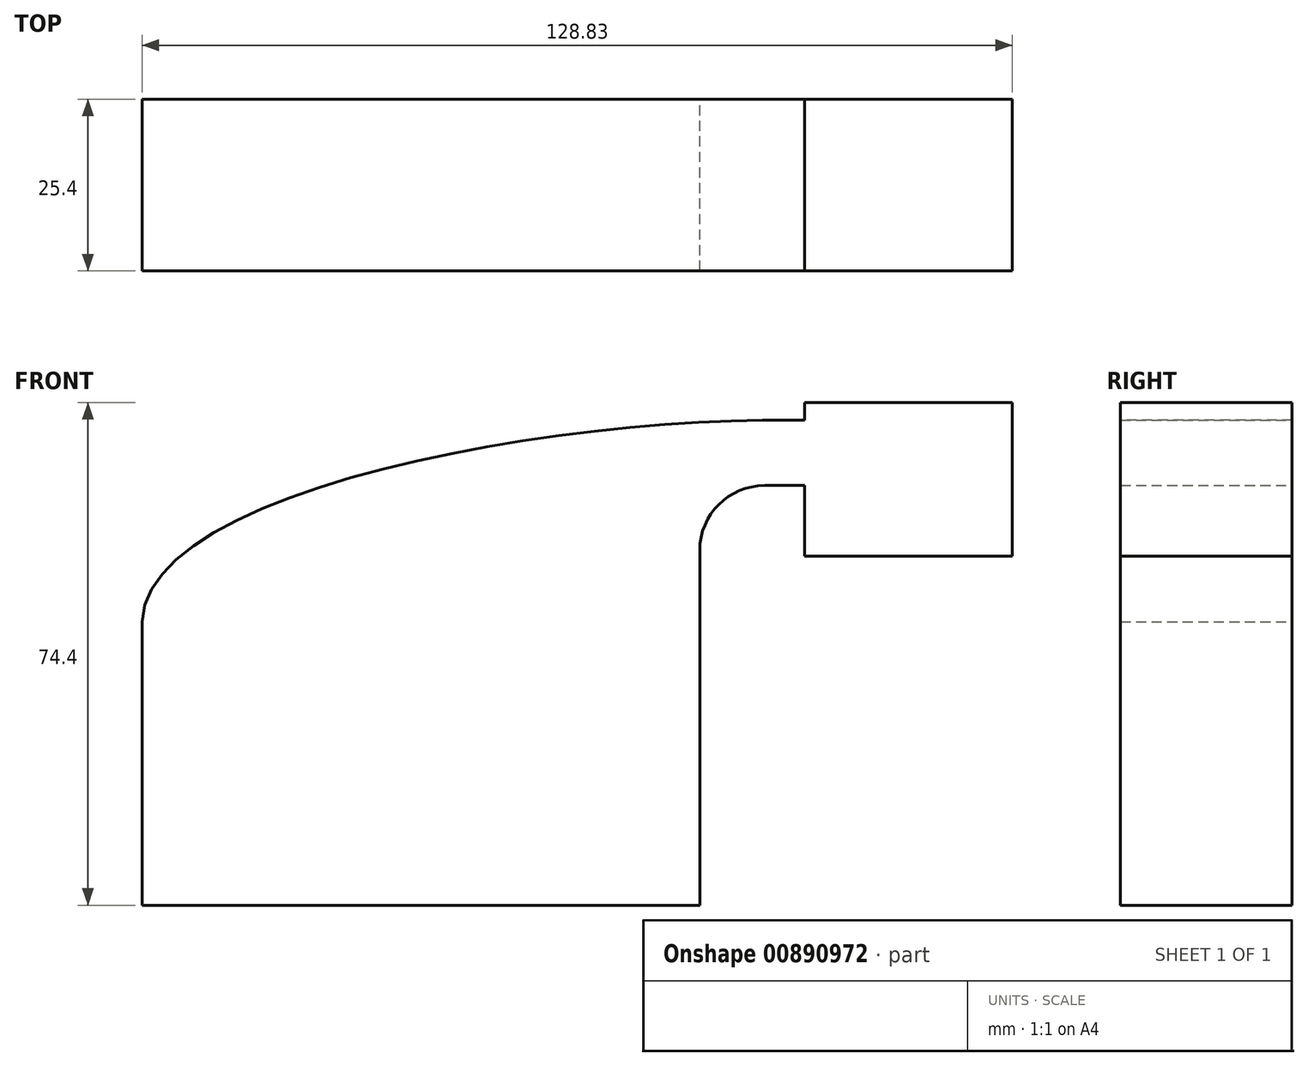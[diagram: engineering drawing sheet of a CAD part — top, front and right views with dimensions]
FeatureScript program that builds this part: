
annotation { "Feature Type Name" : "Feature", "Feature Type Description" : "" }
export const myFeature = defineFeature(function(context is Context, id is Id, definition is map)
    precondition{}
    {
        {
            var Q0;
            Q0=qCreatedBy(makeId("Front.planeOp"),FACE);
            var sketch = newSketch(context, id + "F0", { "sketchPlane" : qUnion([Q0])});
            skLineSegment(sketch, "E0.bottom", {"start": v(-41.27, 20.98) * mm, "end": v(41.27, 20.98) * mm});
            skLineSegment(sketch, "E0.top", {"start": v(-41.27, -20.98) * mm, "end": v(41.27, -20.98) * mm});
            skLineSegment(sketch, "E0.left", {"start": v(-41.28, 20.98) * mm, "end": v(-41.28, -20.98) * mm});
            skLineSegment(sketch, "E0.right", {"start": v(41.28, 20.98) * mm, "end": v(41.28, -20.98) * mm});
            skPoint(sketch, "E0.middle", {"position": v(0, 0) * mm});
            skLineSegment(sketch, "E1.bottom", {"start": v(56.8, 30.67) * mm, "end": v(87.55, 30.67) * mm});
            skLineSegment(sketch, "E1.top", {"start": v(56.8, 53.42) * mm, "end": v(87.55, 53.42) * mm});
            skLineSegment(sketch, "E1.left", {"start": v(56.8, 30.67) * mm, "end": v(56.8, 53.42) * mm});
            skLineSegment(sketch, "E1.right", {"start": v(87.55, 30.67) * mm, "end": v(87.55, 53.42) * mm});
            skPoint(sketch, "E1.middle", {"position": v(72.17, 42.04) * mm});
            skLineSegment(sketch, "E2", {"start": v(41.28, 20.98) * mm, "end": v(41.28, 31.55) * mm});
            skArc(sketch, "E3", {"start": v(41.28, 31.55) * mm, "mid": v(44.08, 38.33) * mm, "end": v(50.86, 41.13) * mm});
            skLineSegment(sketch, "E4", {"start": v(50.86, 41.13) * mm, "end": v(72.44, 41.13) * mm});
            skLineSegment(sketch, "E5.0", {"start": v(50.86, 50.79) * mm, "end": v(72.43, 50.79) * mm});
            skArc(sketch, "E5.1", {"start": v(31.62, 31.55) * mm, "mid": v(37.26, 45.15) * mm, "end": v(50.86, 50.79) * mm});
            skLineSegment(sketch, "E5.2", {"start": v(31.62, 20.98) * mm, "end": v(31.62, 31.55) * mm});
            skFitSpline(sketch, "E6", {"points": [v(-41.28, 20.98) * mm, v(50.86, 50.79) * mm], "startDerivative": vector(2.45, 57.64) * mm, "endDerivative": vector(103.54, 0.79) * mm});
            skSolve(sketch);
        }
        {
            var Q0;
            Q0=makeQuery(id+"F0.imprint","IMPRINT",FACE,{"disambiguationData":[TD([[makeQuery(id+"F0.imprint","IMPRINT",EDGE,{"derivedFrom":sQuery(id+"F0.wireOp",EDGE,"E0.top")}),1.0]])]});
            var Q1;
            {var subQ3=sQuery(id+"F0.wireOp",EDGE,"E5.2");Q1=makeQuery(id+"F0.imprint","IMPRINT",FACE,{"disambiguationData":[TD([[makeQuery(id+"F0.imprint","IMPRINT",EDGE,{"derivedFrom":subQ3}),1.0]])]});}
            var Q2;
            {var subQ1=sQuery(id+"F0.wireOp",EDGE,"E2");Q2=makeQuery(id+"F0.imprint","IMPRINT",FACE,{"disambiguationData":[TD([[makeQuery(id+"F0.imprint","IMPRINT",EDGE,{"derivedFrom":subQ1}),1.0]])]});}
            var Q3;
            {var subQ3=sQuery(id+"F0.wireOp",EDGE,"E1.bottom");Q3=makeQuery(id+"F0.imprint","IMPRINT",FACE,{"disambiguationData":[TD([[makeQuery(id+"F0.imprint","IMPRINT",EDGE,{"derivedFrom":subQ3}),1.0]])]});}
            extrude(context, id + "F1", {"entities" : qUnion([Q0, Q1, Q2, Q3]), "endBound" : BoundingType.SYMMETRIC, "depth" : 25.4 * mm, "offsetDistance" : 25.4 * mm});
        }
    });
